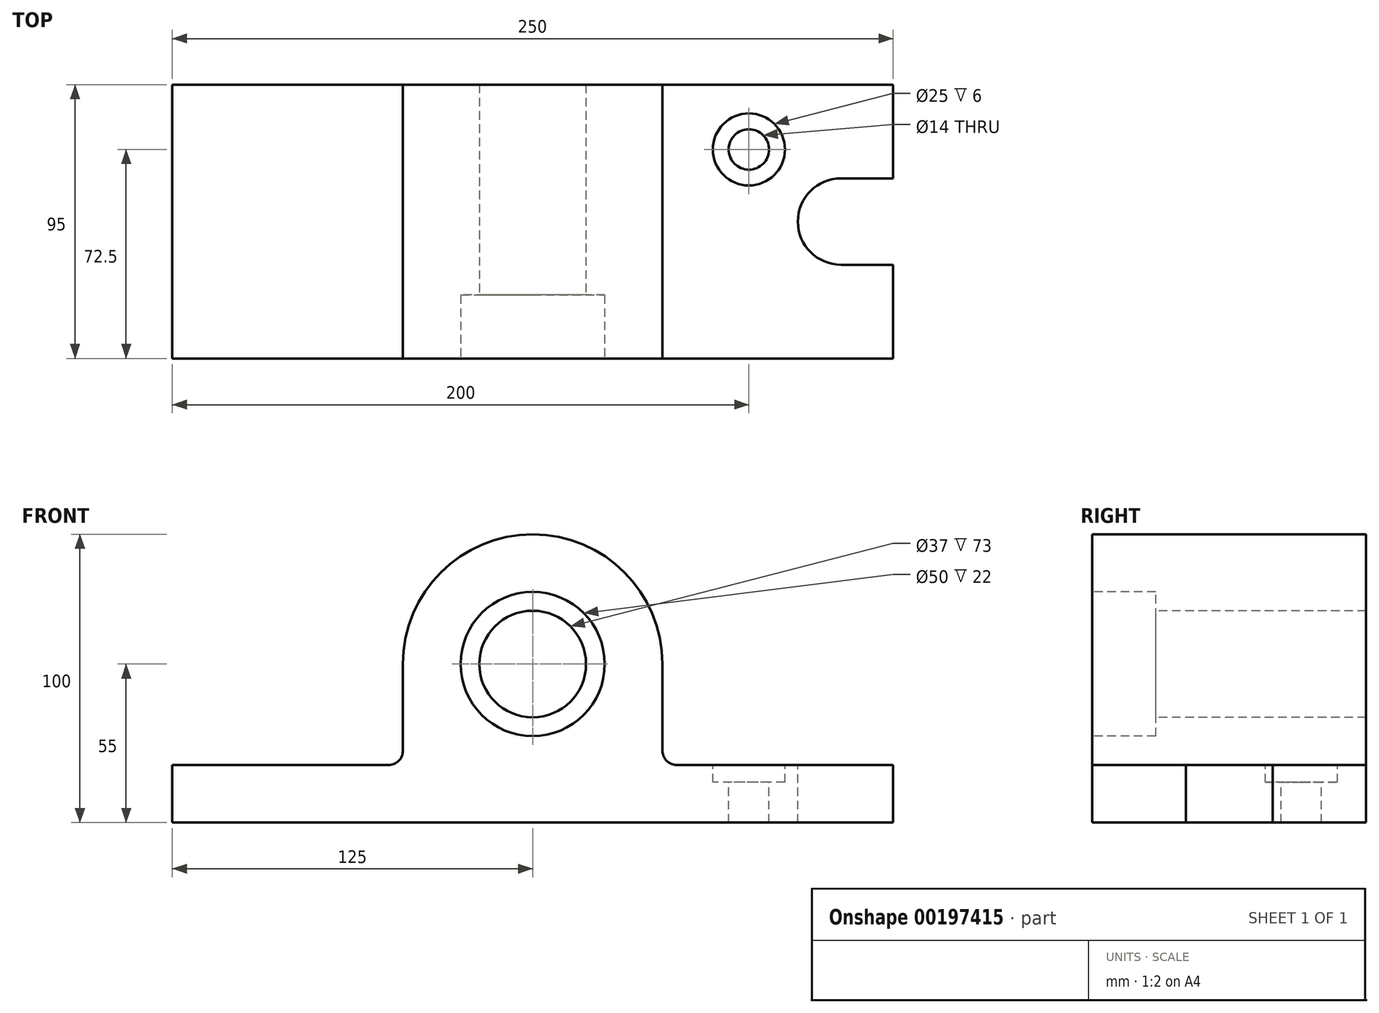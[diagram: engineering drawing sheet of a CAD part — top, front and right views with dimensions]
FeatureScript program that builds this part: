
annotation { "Feature Type Name" : "Feature", "Feature Type Description" : "" }
export const myFeature = defineFeature(function(context is Context, id is Id, definition is map)
    precondition{}
    {
        {
            var Q0;
            Q0=qCreatedBy(makeId("Front.planeOp"),FACE);
            var sketch = newSketch(context, id + "F0", { "sketchPlane" : qUnion([Q0])});
            skLineSegment(sketch, "E0.bottom", {"start": v(-125, 10) * mm, "end": v(-45, 10) * mm});
            skLineSegment(sketch, "E0.top", {"start": v(-125, -10) * mm, "end": v(125, -10) * mm});
            skLineSegment(sketch, "E0.left", {"start": v(-125, 10) * mm, "end": v(-125, -10) * mm});
            skLineSegment(sketch, "E0.right", {"start": v(125, 10) * mm, "end": v(125, -10) * mm});
            skPoint(sketch, "E0.middle", {"position": v(0, 0) * mm});
            skLineSegment(sketch, "E1.trimOffspring", {"start": v(45, 10) * mm, "end": v(125, 10) * mm});
            skLineSegment(sketch, "E2.top", {"start": v(-45, 90) * mm, "end": v(45, 90) * mm});
            skLineSegment(sketch, "E2.left", {"start": v(-45, 10) * mm, "end": v(-45, 90) * mm});
            skLineSegment(sketch, "E2.right", {"start": v(45, 10) * mm, "end": v(45, 90) * mm});
            skSolve(sketch);
        }
        {
            var Q0;
            Q0=makeQuery(id+"F0.imprint","IMPRINT",FACE,{"disambiguationData":[TD([[makeQuery(id+"F0.imprint","IMPRINT",EDGE,{"derivedFrom":sQuery(id+"F0.wireOp",EDGE,"E0.bottom")}),-1.0]])]});
            extrude(context, id + "F1", {"entities" : qUnion([Q0]), "endBound" : BoundingType.SYMMETRIC, "depth" : 95 * mm});
        }
        {
            var Q0;
            Q0=makeQuery(id+"F1.opExtrude","SWEPT_EDGE",EDGE,{"disambiguationData":[OSD([sQuery(id+"F0.wireOp",EDGE,"E2.top"),sQuery(id+"F0.wireOp",EDGE,"E2.right")])]});
            var Q1;
            Q1=makeQuery(id+"F1.opExtrude","SWEPT_EDGE",EDGE,{"disambiguationData":[OSD([sQuery(id+"F0.wireOp",EDGE,"E2.top"),sQuery(id+"F0.wireOp",EDGE,"E2.left")])]});
            fillet(context, id + "F2", {"entities" : qUnion([Q0, Q1]), "radius" : 45 * mm, "tangentPropagation" : true, "allowEdgeOverflow" : false});
        }
        {
            var Q0;
            Q0=makeQuery(id+"F1.opExtrude","SWEPT_EDGE",EDGE,{"disambiguationData":[OSD([sQuery(id+"F0.wireOp",EDGE,"E1.trimOffspring"),sQuery(id+"F0.wireOp",EDGE,"E2.right")])]});
            var Q1;
            Q1=makeQuery(id+"F1.opExtrude","SWEPT_EDGE",EDGE,{"disambiguationData":[OSD([sQuery(id+"F0.wireOp",EDGE,"E0.bottom"),sQuery(id+"F0.wireOp",EDGE,"E2.left")])]});
            fillet(context, id + "F3", {"entities" : qUnion([Q0, Q1]), "radius" : 5 * mm, "tangentPropagation" : true, "allowEdgeOverflow" : false});
        }
        {
            var Q0;
            Q0=makeQuery(id+"F1.opExtrude","CAP_FACE",FACE,{"disambiguationData":[OSD([sQuery(id+"F0.wireOp",EDGE,"E0.bottom"),sQuery(id+"F0.wireOp",EDGE,"E0.top"),sQuery(id+"F0.wireOp",EDGE,"E0.left"),sQuery(id+"F0.wireOp",EDGE,"E0.right"),sQuery(id+"F0.wireOp",EDGE,"E1.trimOffspring"),sQuery(id+"F0.wireOp",EDGE,"E2.top"),sQuery(id+"F0.wireOp",EDGE,"E2.left"),sQuery(id+"F0.wireOp",EDGE,"E2.right")])],"isStart":false});
            var sketch = newSketch(context, id + "F4", { "sketchPlane" : qUnion([Q0])});
            skCircle(sketch, "E3", {"center": v(0, 45) * mm, "radius": 18.5 * mm});
            skCircle(sketch, "E4", {"center": v(0, 45) * mm, "radius": 25 * mm});
            skSolve(sketch);
        }
        {
            var Q0;
            Q0=makeQuery(id+"F4.imprint","IMPRINT",FACE,{"disambiguationData":[TD([[makeQuery(id+"F4.imprint","IMPRINT",EDGE,{"derivedFrom":sQuery(id+"F4.wireOp",EDGE,"E3")}),1.0]])]});
            extrude(context, id + "F5", {"entities" : qUnion([Q0]), "operationType" : NewBodyOperationType.REMOVE, "endBound" : BoundingType.THROUGH_ALL, "oppositeDirection" : true, "depth" : 25 * mm});
        }
        {
            var Q0;
            Q0=makeQuery(id+"F4.imprint","IMPRINT",FACE,{"disambiguationData":[TD([[makeQuery(id+"F4.imprint","IMPRINT",EDGE,{"derivedFrom":sQuery(id+"F4.wireOp",EDGE,"E3")}),-1.0]])]});
            extrude(context, id + "F6", {"entities" : qUnion([Q0]), "operationType" : NewBodyOperationType.REMOVE, "oppositeDirection" : true, "depth" : 22 * mm});
        }
        {
            var Q0;
            Q0=makeQuery(id+"F1.opExtrude","SWEPT_FACE",FACE,{"disambiguationData":[OSD([sQuery(id+"F0.wireOp",EDGE,"E1.trimOffspring")])]});
            var sketch = newSketch(context, id + "F7", { "sketchPlane" : qUnion([Q0])});
            skCircle(sketch, "E5", {"center": v(75, 25) * mm, "radius": 7 * mm});
            skCircle(sketch, "E6", {"center": v(75, 25) * mm, "radius": 12.5 * mm});
            skLineSegment(sketch, "E7", {"start": v(125, 15) * mm, "end": v(107, 15) * mm});
            skLineSegment(sketch, "E8.MirrorCS", {"start": v(125, -15) * mm, "end": v(107, -15) * mm});
            skArc(sketch, "E9", {"start": v(107, 15) * mm, "mid": v(92, 0) * mm, "end": v(107, -15) * mm});
            skSolve(sketch);
        }
        {
            var Q0;
            {var subQ0=sQuery(id+"F7.wireOp",EDGE,"E7");Q0=makeQuery(id+"F7.imprint","IMPRINT",FACE,{"disambiguationData":[TD([[makeQuery(id+"F7.imprint","IMPRINT",EDGE,{"derivedFrom":subQ0}),1.0]])]});}
            extrude(context, id + "F8", {"entities" : qUnion([Q0]), "operationType" : NewBodyOperationType.REMOVE, "endBound" : BoundingType.THROUGH_ALL, "oppositeDirection" : true, "depth" : 25 * mm});
        }
        {
            var Q0;
            Q0=makeQuery(id+"F7.imprint","IMPRINT",FACE,{"disambiguationData":[TD([[makeQuery(id+"F7.imprint","IMPRINT",EDGE,{"derivedFrom":sQuery(id+"F7.wireOp",EDGE,"E5")}),-1.0]])]});
            extrude(context, id + "F9", {"entities" : qUnion([Q0]), "operationType" : NewBodyOperationType.REMOVE, "oppositeDirection" : true, "depth" : 6 * mm});
        }
        {
            var Q0;
            Q0=makeQuery(id+"F7.imprint","IMPRINT",FACE,{"disambiguationData":[TD([[makeQuery(id+"F7.imprint","IMPRINT",EDGE,{"derivedFrom":sQuery(id+"F7.wireOp",EDGE,"E5")}),1.0]])]});
            extrude(context, id + "F10", {"entities" : qUnion([Q0]), "operationType" : NewBodyOperationType.REMOVE, "endBound" : BoundingType.THROUGH_ALL, "oppositeDirection" : true, "depth" : 25 * mm});
        }
    });
